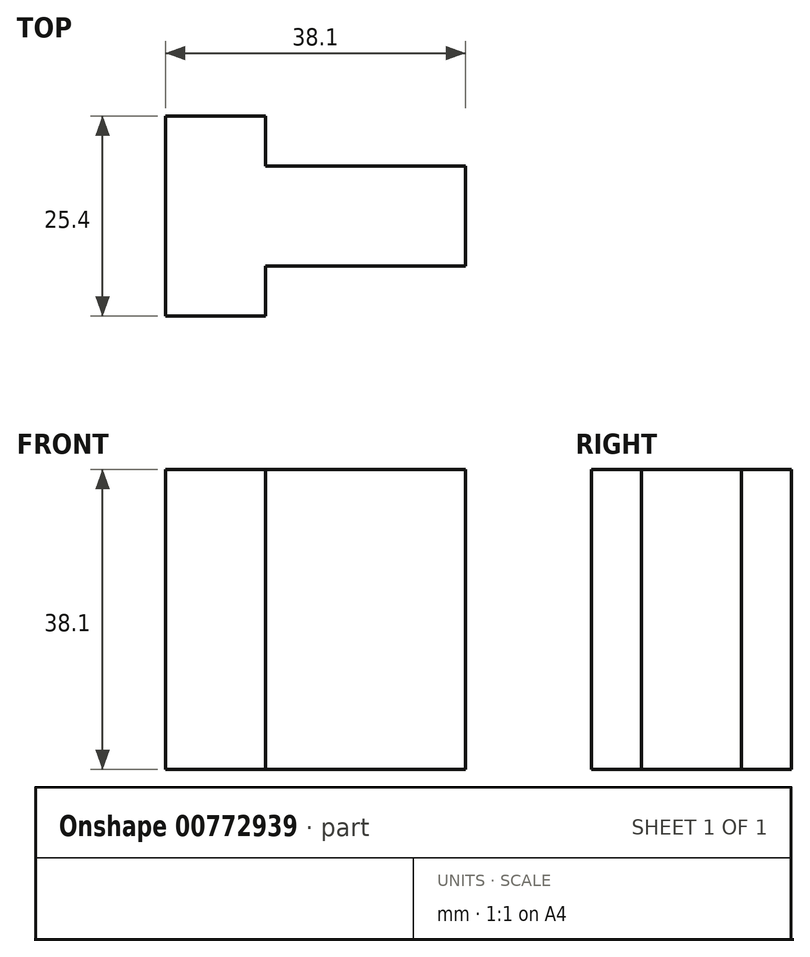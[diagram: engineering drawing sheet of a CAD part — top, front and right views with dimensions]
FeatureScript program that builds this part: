
annotation { "Feature Type Name" : "Feature", "Feature Type Description" : "" }
export const myFeature = defineFeature(function(context is Context, id is Id, definition is map)
    precondition{}
    {
        {
            var Q0;
            Q0=qCreatedBy(makeId("Top.planeOp"),FACE);
            var sketch = newSketch(context, id + "F0", { "sketchPlane" : qUnion([Q0])});
            skLineSegment(sketch, "E0", {"start": v(0, 0) * mm, "end": v(0, 12.7) * mm});
            skLineSegment(sketch, "E1", {"start": v(0, 12.7) * mm, "end": v(-25.4, 12.7) * mm});
            skLineSegment(sketch, "E2", {"start": v(-25.4, 12.7) * mm, "end": v(-25.4, 19.05) * mm});
            skLineSegment(sketch, "E3", {"start": v(-25.4, 19.05) * mm, "end": v(-38.1, 19.05) * mm});
            skLineSegment(sketch, "E4", {"start": v(-38.1, 19.05) * mm, "end": v(-38.1, -6.35) * mm});
            skLineSegment(sketch, "E5", {"start": v(-38.1, -6.35) * mm, "end": v(-25.4, -6.35) * mm});
            skLineSegment(sketch, "E6", {"start": v(-25.4, -6.35) * mm, "end": v(-25.4, 0) * mm});
            skLineSegment(sketch, "E7", {"start": v(-25.4, 0) * mm, "end": v(0, 0) * mm});
            skSolve(sketch);
        }
        {
            var Q0;
            Q0=makeQuery(id+"F0.imprint","IMPRINT",FACE,{"disambiguationData":[TD([[makeQuery(id+"F0.imprint","IMPRINT",EDGE,{"derivedFrom":sQuery(id+"F0.wireOp",EDGE,"E0")}),1.0]])]});
            extrude(context, id + "F1", {"entities" : qUnion([Q0]), "depth" : 38.1 * mm, "offsetDistance" : 25.4 * mm});
        }
    });
